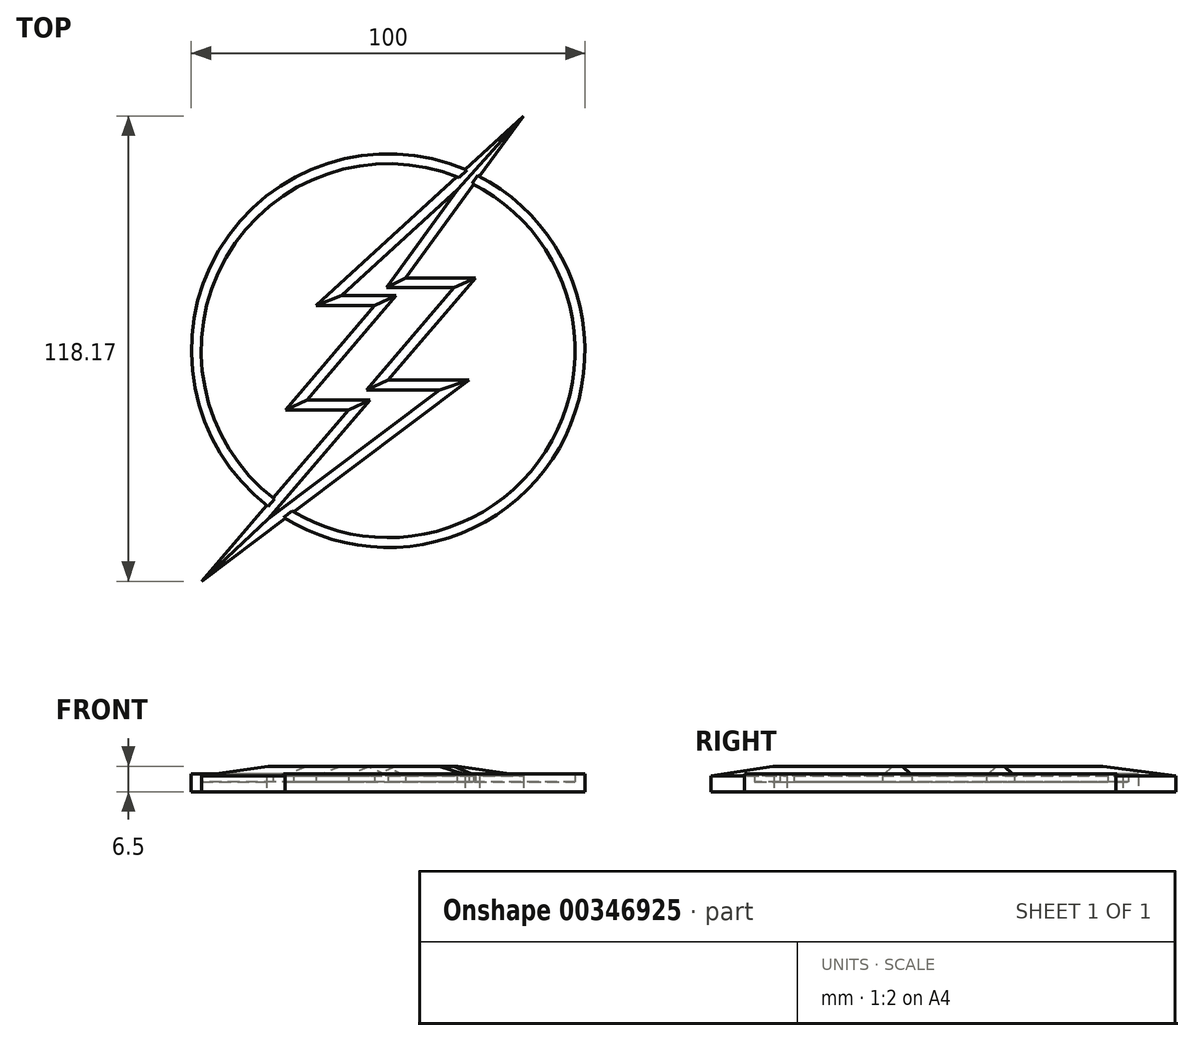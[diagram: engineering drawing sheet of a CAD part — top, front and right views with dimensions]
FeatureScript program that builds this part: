
annotation { "Feature Type Name" : "Feature", "Feature Type Description" : "" }
export const myFeature = defineFeature(function(context is Context, id is Id, definition is map)
    precondition{}
    {
        {
            var Q0;
            Q0=qCreatedBy(makeId("Top.planeOp"),FACE);
            var sketch = newSketch(context, id + "F0", { "sketchPlane" : qUnion([Q0])});
            skCircle(sketch, "E0", {"center": v(0, 0) * mm, "radius": 50 * mm});
            skCircle(sketch, "E1", {"center": v(0, 0) * mm, "radius": 47.5 * mm});
            skSolve(sketch);
        }
        {
            var Q0;
            Q0=makeQuery(id+"F0.imprint","IMPRINT",FACE,{"disambiguationData":[TD([[makeQuery(id+"F0.imprint","IMPRINT",EDGE,{"derivedFrom":sQuery(id+"F0.wireOp",EDGE,"E1")}),1.0]])]});
            extrude(context, id + "F1", {"entities" : qUnion([Q0]), "depth" : 2.5 * mm});
        }
        {
            var Q0;
            Q0=makeQuery(id+"F0.imprint","IMPRINT",FACE,{"disambiguationData":[TD([[makeQuery(id+"F0.imprint","IMPRINT",EDGE,{"derivedFrom":sQuery(id+"F0.wireOp",EDGE,"E0")}),1.0]])]});
            extrude(context, id + "F2", {"entities" : qUnion([Q0]), "operationType" : NewBodyOperationType.ADD, "depth" : 4.5 * mm});
        }
        {
            var Q0;
            Q0=makeQuery(id+"F1.opExtrude","CAP_FACE",FACE,{"disambiguationData":[OSD([sQuery(id+"F0.wireOp",EDGE,"E1")])],"isStart":false});
            var sketch = newSketch(context, id + "F3", { "sketchPlane" : qUnion([Q0])});
            skLineSegment(sketch, "E2", {"start": v(34.32, 59.59) * mm, "end": v(-18.3, 11.46) * mm});
            skLineSegment(sketch, "E3", {"start": v(-18.3, 11.46) * mm, "end": v(-3.42, 11.46) * mm});
            skLineSegment(sketch, "E4", {"start": v(-3.42, 11.46) * mm, "end": v(-26.1, -15.03) * mm});
            skLineSegment(sketch, "E5", {"start": v(-26.1, -15.03) * mm, "end": v(-10.08, -15.03) * mm});
            skLineSegment(sketch, "E6", {"start": v(-10.08, -15.03) * mm, "end": v(-47.37, -58.58) * mm});
            skLineSegment(sketch, "E7", {"start": v(-47.37, -58.58) * mm, "end": v(20.54, -7.45) * mm});
            skLineSegment(sketch, "E8", {"start": v(20.54, -7.45) * mm, "end": v(0, -7.45) * mm});
            skLineSegment(sketch, "E9", {"start": v(0, -7.45) * mm, "end": v(22.22, 18.5) * mm});
            skLineSegment(sketch, "E10", {"start": v(22.22, 18.5) * mm, "end": v(4.44, 18.5) * mm});
            skLineSegment(sketch, "E11", {"start": v(4.44, 18.5) * mm, "end": v(34.32, 59.59) * mm});
            skSolve(sketch);
        }
        {
            var Q0;
            {var subQ10=sQuery(id+"F3.wireOp",EDGE,"E3");Q0=makeQuery(id+"F3.imprint","IMPRINT",FACE,{"disambiguationData":[TD([[makeQuery(id+"F3.imprint","IMPRINT",EDGE,{"derivedFrom":subQ10}),1.0]])]});}
            extrude(context, id + "F4", {"entities" : qUnion([Q0]), "operationType" : NewBodyOperationType.ADD, "depth" : 2.5 * mm});
        }
        {
            var Q0;
            {var subQ0=sQuery(id+"F3.wireOp",EDGE,"E7");var subQ1=sQuery(id+"F3.wireOp",EDGE,"E6");var subQ2=makeQuery(id+"F3.imprint","INTERSECT",VERTEX,{"derivedFrom":[subQ1,subQ0]});Q0=makeQuery(id+"F3.imprint","IMPRINT",FACE,{"disambiguationData":[TD([[makeQuery(id+"F3.imprint","IMPRINT",EDGE,{"disambiguationData":[TD([[subQ2,1.0]])],"derivedFrom":subQ1}),1.0]])]});}
            extrude(context, id + "F5", {"entities" : qUnion([Q0]), "operationType" : NewBodyOperationType.ADD, "depth" : 2.5 * mm});
        }
        {
            var Q0;
            {var subQ0=sQuery(id+"F3.wireOp",EDGE,"E11");var subQ1=sQuery(id+"F3.wireOp",EDGE,"E2");var subQ2=makeQuery(id+"F3.imprint","INTERSECT",VERTEX,{"derivedFrom":[subQ1,subQ0]});Q0=makeQuery(id+"F3.imprint","IMPRINT",FACE,{"disambiguationData":[TD([[makeQuery(id+"F3.imprint","IMPRINT",EDGE,{"disambiguationData":[TD([[subQ2,-1.0]])],"derivedFrom":subQ1}),1.0]])]});}
            extrude(context, id + "F6", {"entities" : qUnion([Q0]), "operationType" : NewBodyOperationType.ADD, "depth" : 2.5 * mm});
        }
        {
            var Q0;
            {var subQ0=sQuery(id+"F3.wireOp",EDGE,"E7");var subQ1=sQuery(id+"F3.wireOp",EDGE,"E6");var subQ2=makeQuery(id+"F3.imprint","INTERSECT",VERTEX,{"derivedFrom":[subQ1,subQ0]});Q0=makeQuery(id+"F3.imprint","IMPRINT",FACE,{"disambiguationData":[TD([[makeQuery(id+"F3.imprint","IMPRINT",EDGE,{"disambiguationData":[TD([[subQ2,1.0]])],"derivedFrom":subQ1}),1.0]])]});}
            extrude(context, id + "F7", {"entities" : qUnion([Q0]), "operationType" : NewBodyOperationType.ADD, "oppositeDirection" : true, "depth" : 2.5 * mm});
        }
        {
            var Q0;
            {var subQ0=sQuery(id+"F3.wireOp",EDGE,"E11");var subQ1=sQuery(id+"F3.wireOp",EDGE,"E2");var subQ2=makeQuery(id+"F3.imprint","INTERSECT",VERTEX,{"derivedFrom":[subQ1,subQ0]});Q0=makeQuery(id+"F3.imprint","IMPRINT",FACE,{"disambiguationData":[TD([[makeQuery(id+"F3.imprint","IMPRINT",EDGE,{"disambiguationData":[TD([[subQ2,-1.0]])],"derivedFrom":subQ1}),1.0]])]});}
            extrude(context, id + "F8", {"entities" : qUnion([Q0]), "operationType" : NewBodyOperationType.ADD, "oppositeDirection" : true, "depth" : 2.5 * mm});
        }
        {
            var Q0;
            {var subQ0=sQuery(id+"F3.wireOp",EDGE,"E11");var subQ1=sQuery(id+"F3.wireOp",EDGE,"E2");var subQ2=sQuery(id+"F0.wireOp",EDGE,"E1");var subQ3=sQuery(id+"F3.wireOp",EDGE,"E7");var subQ4=sQuery(id+"F3.wireOp",EDGE,"E6");Q0=makeQuery(id+"F6.boolean.opBoolean","MERGE",FACE,{"derivedFrom":[makeQuery(id+"F5.boolean.opBoolean","MERGE",FACE,{"derivedFrom":[makeQuery(id+"F4.opExtrude","CAP_FACE",FACE,{"disambiguationData":[OSD([subQ2,subQ1,sQuery(id+"F3.wireOp",EDGE,"E3"),sQuery(id+"F3.wireOp",EDGE,"E4"),sQuery(id+"F3.wireOp",EDGE,"E5"),subQ4,subQ3,sQuery(id+"F3.wireOp",EDGE,"E8"),sQuery(id+"F3.wireOp",EDGE,"E9"),sQuery(id+"F3.wireOp",EDGE,"E10"),subQ0])],"isStart":false}),makeQuery(id+"F5.opExtrude","CAP_FACE",FACE,{"disambiguationData":[OSD([subQ2,subQ4,subQ3])],"isStart":false})]}),makeQuery(id+"F6.opExtrude","CAP_FACE",FACE,{"disambiguationData":[OSD([subQ2,subQ1,subQ0])],"isStart":false})]});}
            extrude(context, id + "F9", {"entities" : qUnion([Q0]), "operationType" : NewBodyOperationType.ADD, "depth" : 1.5 * mm});
        }
        {
            var Q0;
            Q0=makeQuery(id+"F9.opExtrude","CAP_EDGE",EDGE,{"disambiguationData":[OSD([sQuery(id+"F3.wireOp",EDGE,"E7")])],"isStart":false});
            chamfer(context, id + "F10", {"entities" : qUnion([Q0]), "width" : 2.5 * mm, "tangentPropagation" : true});
        }
        {
            var Q0;
            Q0=makeQuery(id+"F9.opExtrude","CAP_EDGE",EDGE,{"disambiguationData":[OSD([sQuery(id+"F3.wireOp",EDGE,"E6")])],"isStart":false});
            chamfer(context, id + "F11", {"entities" : qUnion([Q0]), "width" : 2.5 * mm, "tangentPropagation" : true});
        }
        {
            var Q0;
            Q0=makeQuery(id+"F9.opExtrude","CAP_EDGE",EDGE,{"disambiguationData":[OSD([sQuery(id+"F3.wireOp",EDGE,"E8")])],"isStart":false});
            chamfer(context, id + "F12", {"entities" : qUnion([Q0]), "width" : 2.5 * mm, "tangentPropagation" : true});
        }
        {
            var Q0;
            Q0=makeQuery(id+"F9.opExtrude","CAP_EDGE",EDGE,{"disambiguationData":[OSD([sQuery(id+"F3.wireOp",EDGE,"E5")])],"isStart":false});
            chamfer(context, id + "F13", {"entities" : qUnion([Q0]), "width" : 2.5 * mm, "tangentPropagation" : true});
        }
        {
            var Q0;
            Q0=makeQuery(id+"F9.opExtrude","CAP_EDGE",EDGE,{"disambiguationData":[OSD([sQuery(id+"F3.wireOp",EDGE,"E4")])],"isStart":false});
            chamfer(context, id + "F14", {"entities" : qUnion([Q0]), "width" : 2.5 * mm, "tangentPropagation" : true});
        }
        {
            var Q0;
            Q0=makeQuery(id+"F9.opExtrude","CAP_EDGE",EDGE,{"disambiguationData":[OSD([sQuery(id+"F3.wireOp",EDGE,"E9")])],"isStart":false});
            chamfer(context, id + "F15", {"entities" : qUnion([Q0]), "width" : 2.5 * mm, "tangentPropagation" : true});
        }
        {
            var Q0;
            Q0=makeQuery(id+"F9.opExtrude","CAP_EDGE",EDGE,{"disambiguationData":[OSD([sQuery(id+"F3.wireOp",EDGE,"E3")])],"isStart":false});
            chamfer(context, id + "F16", {"entities" : qUnion([Q0]), "width" : 2.5 * mm, "tangentPropagation" : true});
        }
        {
            var Q0;
            Q0=makeQuery(id+"F9.opExtrude","CAP_EDGE",EDGE,{"disambiguationData":[OSD([sQuery(id+"F3.wireOp",EDGE,"E10")])],"isStart":false});
            chamfer(context, id + "F17", {"entities" : qUnion([Q0]), "width" : 2.5 * mm, "tangentPropagation" : true});
        }
        {
            var Q0;
            Q0=makeQuery(id+"F9.opExtrude","CAP_EDGE",EDGE,{"disambiguationData":[OSD([sQuery(id+"F3.wireOp",EDGE,"E2")])],"isStart":false});
            chamfer(context, id + "F18", {"entities" : qUnion([Q0]), "width" : 2.5 * mm, "tangentPropagation" : true});
        }
        {
            var Q0;
            Q0=makeQuery(id+"F9.opExtrude","CAP_EDGE",EDGE,{"disambiguationData":[OSD([sQuery(id+"F3.wireOp",EDGE,"E11")])],"isStart":false});
            chamfer(context, id + "F19", {"entities" : qUnion([Q0]), "width" : 2.5 * mm, "tangentPropagation" : true});
        }
    });
